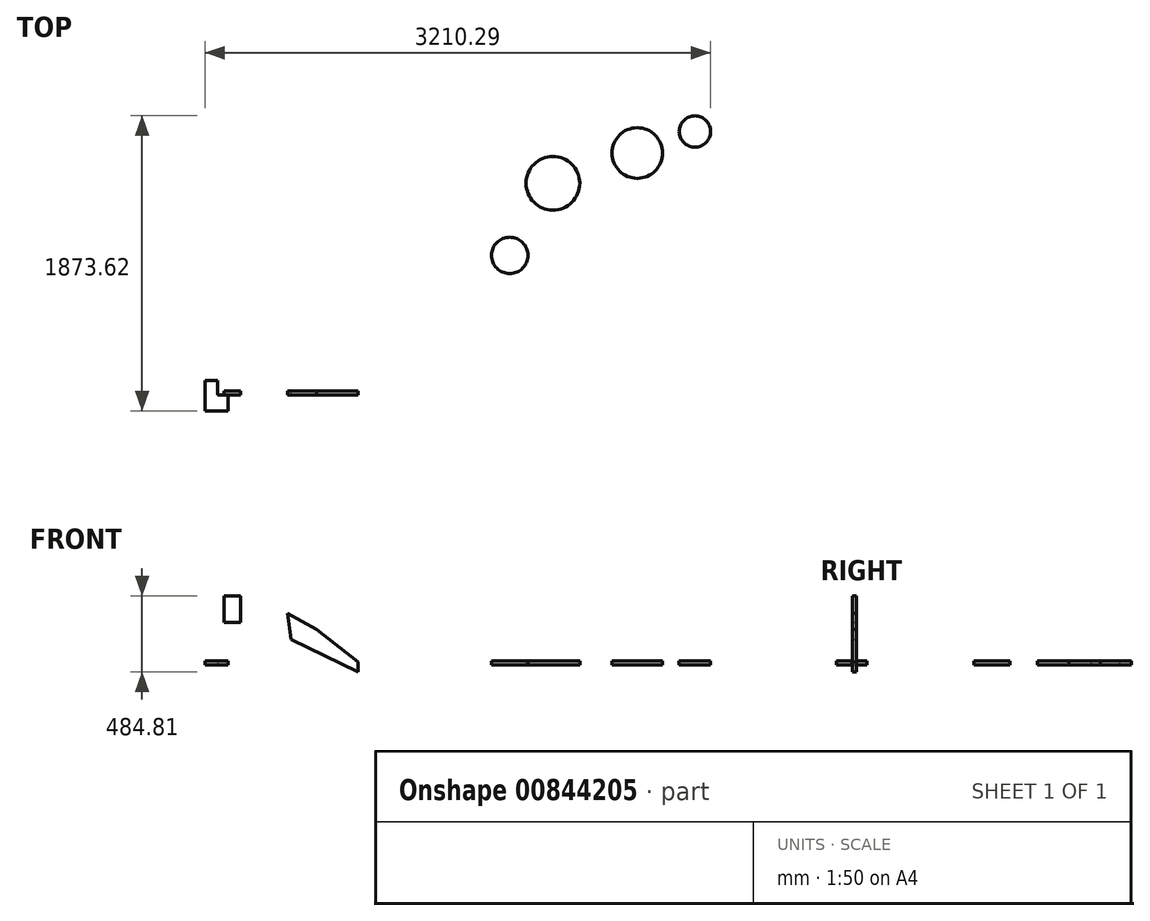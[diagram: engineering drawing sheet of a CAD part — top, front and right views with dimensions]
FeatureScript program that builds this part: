
annotation { "Feature Type Name" : "Feature", "Feature Type Description" : "" }
export const myFeature = defineFeature(function(context is Context, id is Id, definition is map)
    precondition{}
    {
        {
            var Q0;
            Q0=qCreatedBy(makeId("Top.planeOp"),FACE);
            var sketch = newSketch(context, id + "F0", { "sketchPlane" : qUnion([Q0])});
            skLineSegment(sketch, "E0.bottom", {"start": v(-168.34, -125.92) * mm, "end": v(-23.53, -125.92) * mm});
            skLineSegment(sketch, "E0.top", {"start": v(-168.34, -26.64) * mm, "end": v(-23.53, -26.64) * mm});
            skLineSegment(sketch, "E0.left", {"start": v(-168.34, -125.92) * mm, "end": v(-168.34, -26.64) * mm});
            skLineSegment(sketch, "E0.right", {"start": v(-23.53, -125.92) * mm, "end": v(-23.53, -26.64) * mm});
            skLineSegment(sketch, "E1.bottom", {"start": v(-168.34, -26.64) * mm, "end": v(-89.27, -26.64) * mm});
            skLineSegment(sketch, "E1.top", {"start": v(-168.34, 0) * mm, "end": v(-89.27, 0) * mm});
            skLineSegment(sketch, "E1.left", {"start": v(-168.34, -26.64) * mm, "end": v(-168.34, 0) * mm});
            skLineSegment(sketch, "E1.right", {"start": v(-89.27, -26.64) * mm, "end": v(-89.27, 0) * mm});
            skLineSegment(sketch, "E2.bottom", {"start": v(-89.27, 0) * mm, "end": v(-168.34, 0) * mm});
            skLineSegment(sketch, "E2.top", {"start": v(-89.27, 66.4) * mm, "end": v(-168.34, 66.4) * mm});
            skLineSegment(sketch, "E2.left", {"start": v(-89.27, 0) * mm, "end": v(-89.27, 66.4) * mm});
            skLineSegment(sketch, "E2.right", {"start": v(-168.34, 0) * mm, "end": v(-168.34, 66.4) * mm});
            skSolve(sketch);
        }
        {
            var Q0;
            Q0 = qSketchRegion(id + "F0", true);
            extrude(context, id + "F1", {"entities" : qUnion([Q0]), "depth" : 25.4 * mm, "offsetDistance" : 25.4 * mm});
        }
        {
            var Q0;
            Q0=qCreatedBy(makeId("Front.planeOp"),FACE);
            var sketch = newSketch(context, id + "F2", { "sketchPlane" : qUnion([Q0])});
            skLineSegment(sketch, "E3.bottom", {"start": v(-46.46, 269.26) * mm, "end": v(4.71, 269.26) * mm});
            skLineSegment(sketch, "E3.top", {"start": v(-46.46, 325.9) * mm, "end": v(4.71, 325.9) * mm});
            skLineSegment(sketch, "E3.left", {"start": v(-46.46, 269.26) * mm, "end": v(-46.46, 325.9) * mm});
            skLineSegment(sketch, "E3.right", {"start": v(4.71, 269.26) * mm, "end": v(4.71, 325.9) * mm});
            skLineSegment(sketch, "E4.bottom", {"start": v(4.71, 325.9) * mm, "end": v(56.12, 325.9) * mm});
            skLineSegment(sketch, "E4.top", {"start": v(4.71, 438.13) * mm, "end": v(56.12, 438.13) * mm});
            skLineSegment(sketch, "E4.left", {"start": v(4.71, 325.9) * mm, "end": v(4.71, 438.13) * mm});
            skLineSegment(sketch, "E4.right", {"start": v(56.12, 325.9) * mm, "end": v(56.12, 438.13) * mm});
            skLineSegment(sketch, "E5.bottom", {"start": v(4.71, 438.13) * mm, "end": v(-46.46, 438.13) * mm});
            skLineSegment(sketch, "E5.top", {"start": v(4.71, 325.9) * mm, "end": v(-46.46, 325.9) * mm});
            skLineSegment(sketch, "E5.left", {"start": v(4.71, 438.13) * mm, "end": v(4.71, 325.9) * mm});
            skLineSegment(sketch, "E5.right", {"start": v(-46.46, 438.13) * mm, "end": v(-46.46, 325.9) * mm});
            skLineSegment(sketch, "E6.bottom", {"start": v(4.71, 269.26) * mm, "end": v(56.12, 269.26) * mm});
            skLineSegment(sketch, "E6.right", {"start": v(56.12, 269.26) * mm, "end": v(56.12, 325.9) * mm});
            skSolve(sketch);
        }
        {
            var Q0;
            Q0 = qSketchRegion(id + "F2", true);
            extrude(context, id + "F3", {"entities" : qUnion([Q0]), "depth" : 25.4 * mm, "offsetDistance" : 25.4 * mm});
        }
        {
            var Q0;
            Q0=qCreatedBy(makeId("Front.planeOp"),FACE);
            var sketch = newSketch(context, id + "F4", { "sketchPlane" : qUnion([Q0])});
            skLineSegment(sketch, "E7", {"start": v(354.66, 327.1) * mm, "end": v(538.57, 223.4) * mm});
            skLineSegment(sketch, "E8", {"start": v(538.57, 223.4) * mm, "end": v(538.57, 148.02) * mm});
            skLineSegment(sketch, "E9", {"start": v(538.57, 148.02) * mm, "end": v(802.68, 16.94) * mm});
            skLineSegment(sketch, "E10", {"start": v(802.68, 16.94) * mm, "end": v(802.68, -46.68) * mm});
            skLineSegment(sketch, "E11", {"start": v(802.68, -46.68) * mm, "end": v(378, 160.14) * mm});
            skLineSegment(sketch, "E12", {"start": v(354.66, 327.1) * mm, "end": v(378, 160.14) * mm});
            skLineSegment(sketch, "E13", {"start": v(538.57, 223.4) * mm, "end": v(802.68, 16.94) * mm});
            skSolve(sketch);
        }
        {
            var Q0;
            Q0 = qSketchRegion(id + "F4", true);
            extrude(context, id + "F5", {"entities" : qUnion([Q0]), "depth" : 25.4 * mm, "offsetDistance" : 25.4 * mm});
        }
        {
            var Q0;
            Q0=qCreatedBy(makeId("Top.planeOp"),FACE);
            var sketch = newSketch(context, id + "F6", { "sketchPlane" : qUnion([Q0])});
            skCircle(sketch, "E14", {"center": v(2040.67, 1319) * mm, "radius": 170.44 * mm});
            skCircle(sketch, "E15", {"center": v(2576.43, 1511.16) * mm, "radius": 160.5 * mm});
            skCircle(sketch, "E16", {"center": v(1766.34, 861.06) * mm, "radius": 115.36 * mm});
            skCircle(sketch, "E17", {"center": v(2942.31, 1648.07) * mm, "radius": 99.64 * mm});
            skLineSegment(sketch, "E18", {"start": v(2980.71, 1443.46) * mm, "end": v(2902.28, 1386.74) * mm});
            skLineSegment(sketch, "E19", {"start": v(2902.28, 1386.74) * mm, "end": v(2784.55, 1241.52) * mm});
            skLineSegment(sketch, "E20", {"start": v(2784.55, 1241.52) * mm, "end": v(2482.73, 1005.45) * mm});
            skLineSegment(sketch, "E21", {"start": v(2482.73, 1005.45) * mm, "end": v(2341.68, 942.43) * mm});
            skLineSegment(sketch, "E22", {"start": v(2341.68, 942.43) * mm, "end": v(2195.05, 816.28) * mm});
            skLineSegment(sketch, "E23", {"start": v(2195.05, 816.28) * mm, "end": v(2482.73, 942.43) * mm});
            skLineSegment(sketch, "E24", {"start": v(2479.76, 930.68) * mm, "end": v(2902.28, 1241.52) * mm});
            skLineSegment(sketch, "E25", {"start": v(2918.3, 1249.17) * mm, "end": v(2980.71, 1443.46) * mm});
            skSolve(sketch);
        }
        {
            var Q0;
            Q0 = qSketchRegion(id + "F6", true);
            extrude(context, id + "F7", {"entities" : qUnion([Q0]), "depth" : 25.4 * mm, "offsetDistance" : 25.4 * mm});
        }
    });
